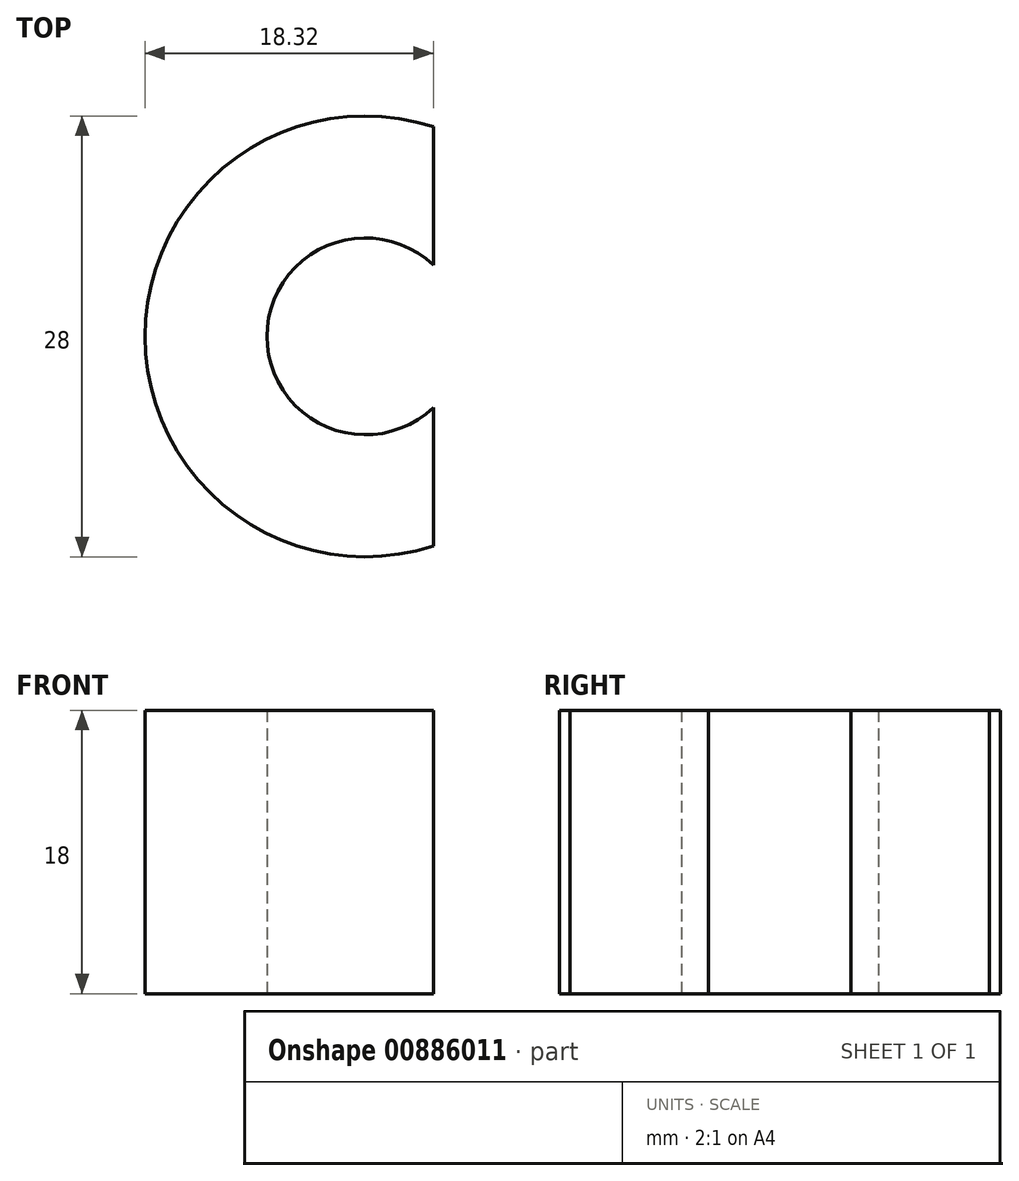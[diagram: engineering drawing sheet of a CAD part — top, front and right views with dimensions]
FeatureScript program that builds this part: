
annotation { "Feature Type Name" : "Feature", "Feature Type Description" : "" }
export const myFeature = defineFeature(function(context is Context, id is Id, definition is map)
    precondition{}
    {
        {
            var Q0;
            Q0=qCreatedBy(makeId("Top.planeOp"),FACE);
            var sketch = newSketch(context, id + "F0", { "sketchPlane" : qUnion([Q0])});
            skCircle(sketch, "E0", {"center": v(0, 0) * mm, "radius": 6.25 * mm});
            skCircle(sketch, "E1", {"center": v(0, 0) * mm, "radius": 14 * mm});
            skLineSegment(sketch, "E2", {"start": v(0, 0) * mm, "end": v(18.12, 0) * mm});
            skCircle(sketch, "E3", {"center": v(18.12, 0) * mm, "radius": 12.04 * mm});
            skLineSegment(sketch, "E4", {"start": v(6.25, 0) * mm, "end": v(6.25, -12.53) * mm});
            skLineSegment(sketch, "E5", {"start": v(6.25, -12.53) * mm, "end": v(6.25, 0) * mm});
            skLineSegment(sketch, "E6", {"start": v(6.25, 12.53) * mm, "end": v(6.25, 0) * mm});
            skLineSegment(sketch, "E7", {"start": v(4.32, -13.32) * mm, "end": v(4.32, 13.32) * mm});
            skSolve(sketch);
        }
        {
            var Q0;
            {var subQ0=sQuery(id+"F0.wireOp",EDGE,"E7");var subQ1=sQuery(id+"F0.wireOp",EDGE,"E0");var subQ2=makeQuery(id+"F0.imprint","INTERSECT",VERTEX,{"disambiguationData":[OD(0.0)],"derivedFrom":[subQ1,subQ0]});Q0=makeQuery(id+"F0.imprint","IMPRINT",FACE,{"disambiguationData":[TD([[makeQuery(id+"F0.imprint","IMPRINT",EDGE,{"disambiguationData":[TD([[subQ2,-1.0]])],"derivedFrom":subQ1}),-1.0]])]});}
            extrude(context, id + "F1", {"entities" : qUnion([Q0]), "depth" : 18 * mm, "offsetDistance" : 25 * mm});
        }
    });
